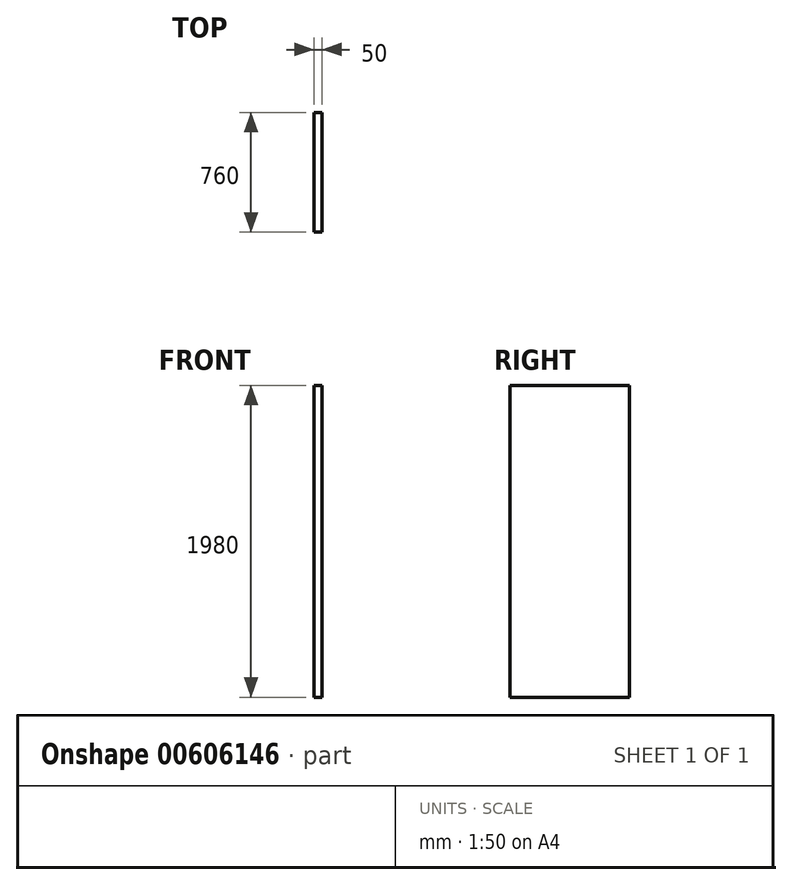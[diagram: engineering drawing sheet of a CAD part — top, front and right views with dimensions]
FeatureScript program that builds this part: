
annotation { "Feature Type Name" : "Feature", "Feature Type Description" : "" }
export const myFeature = defineFeature(function(context is Context, id is Id, definition is map)
    precondition{}
    {
        {
            var Q0;
            Q0=qCreatedBy(makeId("Right.planeOp"),FACE);
            var sketch = newSketch(context, id + "F0", { "sketchPlane" : qUnion([Q0])});
            skLineSegment(sketch, "E0.bottom", {"start": v(-423.37, 1121.08) * mm, "end": v(336.63, 1121.08) * mm});
            skLineSegment(sketch, "E0.top", {"start": v(-423.37, -858.92) * mm, "end": v(336.63, -858.92) * mm});
            skLineSegment(sketch, "E0.left", {"start": v(-423.37, 1121.08) * mm, "end": v(-423.37, -858.92) * mm});
            skLineSegment(sketch, "E0.right", {"start": v(336.63, 1121.08) * mm, "end": v(336.63, -858.92) * mm});
            skSolve(sketch);
        }
        {
            var Q0;
            Q0=qSketchRegion(id+"F0",true);
            extrude(context, id + "F1", {"entities" : qUnion([Q0]), "depth" : 50 * mm, "offsetDistance" : 25 * mm});
        }
    });
